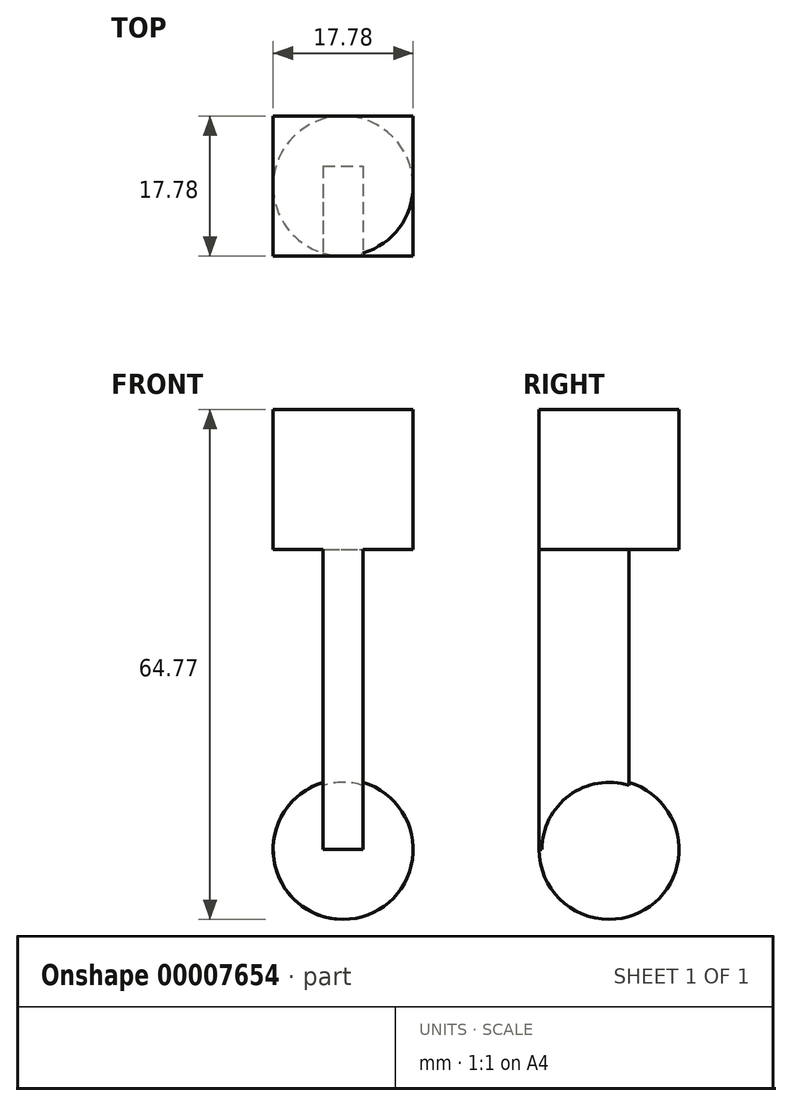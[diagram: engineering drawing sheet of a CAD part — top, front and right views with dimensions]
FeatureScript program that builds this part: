
annotation { "Feature Type Name" : "Feature", "Feature Type Description" : "" }
export const myFeature = defineFeature(function(context is Context, id is Id, definition is map)
    precondition{}
    {
        {
            var Q0;
            Q0=qCreatedBy(makeId("Front.planeOp"),FACE);
            var sketch = newSketch(context, id + "F0", { "sketchPlane" : qUnion([Q0])});
            skCircle(sketch, "E0", {"center": v(0, 0) * mm, "radius": 8.89 * mm});
            skLineSegment(sketch, "E1", {"start": v(0, 8.89) * mm, "end": v(0, -8.89) * mm});
            skSolve(sketch);
        }
        {
            var Q0;
            {var subQ0=sQuery(id+"F0.wireOp",EDGE,"E1");Q0=makeQuery(id+"F0.imprint","IMPRINT",FACE,{"disambiguationData":[TD([[makeQuery(id+"F0.imprint","IMPRINT",EDGE,{"derivedFrom":subQ0}),1.0]])]});}
            var Q1;
            Q1=sQuery(id+"F0.wireOp",EDGE,"E1");
            revolve(context, id + "F1", {"entities" : qUnion([Q0]), "axis" : qUnion([Q1]), "revolveType" : RevolveType.FULL});
        }
        {
            var Q0;
            Q0=qCreatedBy(makeId("Top.planeOp"),FACE);
            var sketch = newSketch(context, id + "F2", { "sketchPlane" : qUnion([Q0])});
            skLineSegment(sketch, "E2.bottom", {"start": v(-2.54, 2.54) * mm, "end": v(2.54, 2.54) * mm});
            skLineSegment(sketch, "E2.top", {"start": v(-2.54, -8.9) * mm, "end": v(2.54, -8.9) * mm});
            skLineSegment(sketch, "E2.left", {"start": v(-2.54, 2.54) * mm, "end": v(-2.54, -8.9) * mm});
            skLineSegment(sketch, "E2.right", {"start": v(2.54, 2.54) * mm, "end": v(2.54, -8.9) * mm});
            skSolve(sketch);
        }
        {
            var Q0;
            Q0 = qSketchRegion(id + "F2", true);
            extrude(context, id + "F3", {"entities" : qUnion([Q0]), "operationType" : NewBodyOperationType.ADD, "depth" : 38.1 * mm});
        }
        {
            var Q0;
            Q0=makeQuery(id+"F3.opExtrude","CAP_FACE",FACE,{"disambiguationData":[OSD([sQuery(id+"F2.wireOp",EDGE,"E2.bottom"),sQuery(id+"F2.wireOp",EDGE,"E2.top"),sQuery(id+"F2.wireOp",EDGE,"E2.left"),sQuery(id+"F2.wireOp",EDGE,"E2.right")])],"isStart":false});
            var sketch = newSketch(context, id + "F4", { "sketchPlane" : qUnion([Q0])});
            skLineSegment(sketch, "E3.bottom", {"start": v(-8.9, 8.9) * mm, "end": v(8.89, 8.9) * mm});
            skLineSegment(sketch, "E3.top", {"start": v(-8.9, -8.89) * mm, "end": v(8.9, -8.89) * mm});
            skLineSegment(sketch, "E3.left", {"start": v(-8.9, 8.9) * mm, "end": v(-8.9, -8.89) * mm});
            skLineSegment(sketch, "E3.right", {"start": v(8.89, 8.9) * mm, "end": v(8.89, -8.89) * mm});
            skSolve(sketch);
        }
        {
            var Q0;
            Q0 = qSketchRegion(id + "F4", true);
            extrude(context, id + "F5", {"entities" : qUnion([Q0]), "operationType" : NewBodyOperationType.ADD, "depth" : 17.78 * mm});
        }
    });
